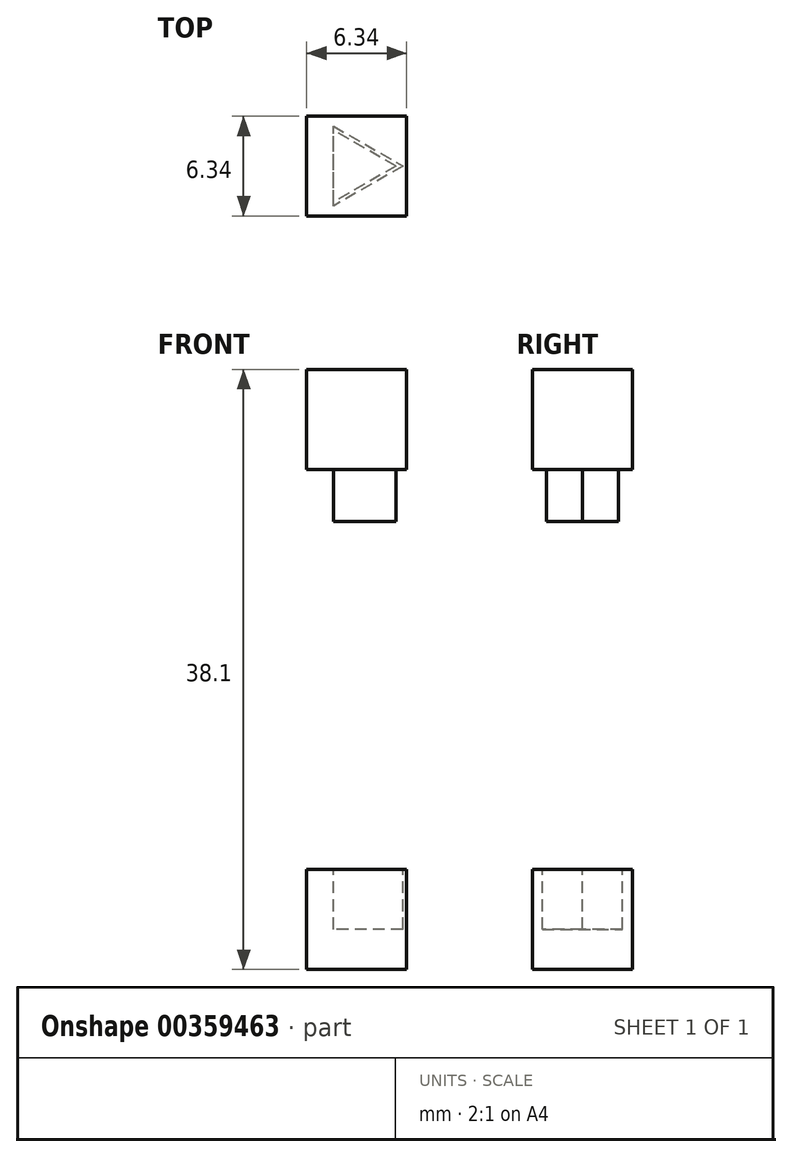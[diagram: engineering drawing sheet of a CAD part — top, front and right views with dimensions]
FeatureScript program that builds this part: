
annotation { "Feature Type Name" : "Feature", "Feature Type Description" : "" }
export const myFeature = defineFeature(function(context is Context, id is Id, definition is map)
    precondition{}
    {
        {
            var Q0;
            Q0=qCreatedBy(makeId("Top.planeOp"),FACE);
            var sketch = newSketch(context, id + "F0", { "sketchPlane" : qUnion([Q0])});
            skLineSegment(sketch, "E0.bottom", {"start": v(-3.18, 3.18) * mm, "end": v(3.18, 3.18) * mm});
            skLineSegment(sketch, "E0.top", {"start": v(-3.18, -3.18) * mm, "end": v(3.17, -3.18) * mm});
            skLineSegment(sketch, "E0.left", {"start": v(-3.17, 3.18) * mm, "end": v(-3.18, -3.18) * mm});
            skLineSegment(sketch, "E0.right", {"start": v(3.18, 3.18) * mm, "end": v(3.17, -3.18) * mm});
            skPoint(sketch, "E0.middle", {"position": v(0, 0) * mm});
            skCircle(sketch, "E1.cCircle", {"center": v(0, 0) * mm, "radius": 1.47 * mm, "construction": true});
            skLineSegment(sketch, "E1.0", {"start": v(-1.47, -2.54) * mm, "end": v(-1.47, 2.54) * mm});
            skLineSegment(sketch, "E1.1", {"start": v(-1.47, 2.54) * mm, "end": v(2.93, 0) * mm});
            skLineSegment(sketch, "E1.2", {"start": v(2.93, 0) * mm, "end": v(-1.47, -2.54) * mm});
            skPoint(sketch, "E1.0.midPoint", {"position": v(-1.47, 0) * mm});
            skSolve(sketch);
        }
        {
            var Q0;
            Q0=makeQuery(id+"F0.imprint","IMPRINT",FACE,{"disambiguationData":[TD([[makeQuery(id+"F0.imprint","IMPRINT",EDGE,{"derivedFrom":sQuery(id+"F0.wireOp",EDGE,"E0.bottom")}),-1.0]])]});
            var Q1;
            Q1=makeQuery(id+"F0.imprint","IMPRINT",FACE,{"disambiguationData":[TD([[makeQuery(id+"F0.imprint","IMPRINT",EDGE,{"derivedFrom":sQuery(id+"F0.wireOp",EDGE,"E1.0")}),-1.0]])]});
            extrude(context, id + "F1", {"entities" : qUnion([Q0, Q1]), "oppositeDirection" : true, "depth" : 6.35 * mm});
        }
        {
            var Q0;
            Q0=makeQuery(id+"F0.imprint","IMPRINT",FACE,{"disambiguationData":[TD([[makeQuery(id+"F0.imprint","IMPRINT",EDGE,{"derivedFrom":sQuery(id+"F0.wireOp",EDGE,"E1.0")}),-1.0]])]});
            extrude(context, id + "F2", {"entities" : qUnion([Q0]), "operationType" : NewBodyOperationType.REMOVE, "oppositeDirection" : true, "depth" : 3.8 * mm});
        }
        {
            var Q0;
            Q0=qCreatedBy(makeId("Top.planeOp"),FACE);
            cPlane(context, id + "F3", {"entities" : qUnion([Q0]), "cplaneType" : CPlaneType.OFFSET, "offset" : 25.4 * mm, "width" : 152.4 * mm, "height" : 152.4 * mm});
        }
        {
            var Q0;
            Q0=qCreatedBy(id+"F3.planeOp",FACE);
            var sketch = newSketch(context, id + "F4", { "sketchPlane" : qUnion([Q0])});
            skLineSegment(sketch, "E2.bottom", {"start": v(-3.18, 3.18) * mm, "end": v(3.18, 3.18) * mm});
            skLineSegment(sketch, "E2.top", {"start": v(-3.18, -3.18) * mm, "end": v(3.18, -3.18) * mm});
            skLineSegment(sketch, "E2.left", {"start": v(-3.18, 3.18) * mm, "end": v(-3.18, -3.18) * mm});
            skLineSegment(sketch, "E2.right", {"start": v(3.18, 3.18) * mm, "end": v(3.18, -3.18) * mm});
            skPoint(sketch, "E2.middle", {"position": v(0, 0) * mm});
            skLineSegment(sketch, "E3", {"start": v(-1.47, 0) * mm, "end": v(-1.47, 2.29) * mm});
            skLineSegment(sketch, "E4", {"start": v(2.5, 0) * mm, "end": v(-1.47, -2.29) * mm});
            skLineSegment(sketch, "E5", {"start": v(-1.47, -2.29) * mm, "end": v(-1.47, 0) * mm});
            skLineSegment(sketch, "E6", {"start": v(2.5, 0) * mm, "end": v(-1.47, 2.29) * mm});
            skSolve(sketch);
        }
        {
            var Q0;
            Q0=makeQuery(id+"F4.imprint","IMPRINT",FACE,{"disambiguationData":[TD([[makeQuery(id+"F4.imprint","IMPRINT",EDGE,{"derivedFrom":sQuery(id+"F4.wireOp",EDGE,"E2.bottom")}),-1.0]])]});
            var Q1;
            Q1=makeQuery(id+"F4.imprint","IMPRINT",FACE,{"disambiguationData":[TD([[makeQuery(id+"F4.imprint","IMPRINT",EDGE,{"derivedFrom":sQuery(id+"F4.wireOp",EDGE,"E3")}),-1.0]])]});
            extrude(context, id + "F5", {"entities" : qUnion([Q0, Q1]), "depth" : 6.35 * mm});
        }
        {
            var Q0;
            Q0=makeQuery(id+"F4.imprint","IMPRINT",FACE,{"disambiguationData":[TD([[makeQuery(id+"F4.imprint","IMPRINT",EDGE,{"derivedFrom":sQuery(id+"F4.wireOp",EDGE,"E3")}),-1.0]])]});
            extrude(context, id + "F6", {"entities" : qUnion([Q0]), "operationType" : NewBodyOperationType.ADD, "oppositeDirection" : true, "depth" : 3.3 * mm});
        }
    });
